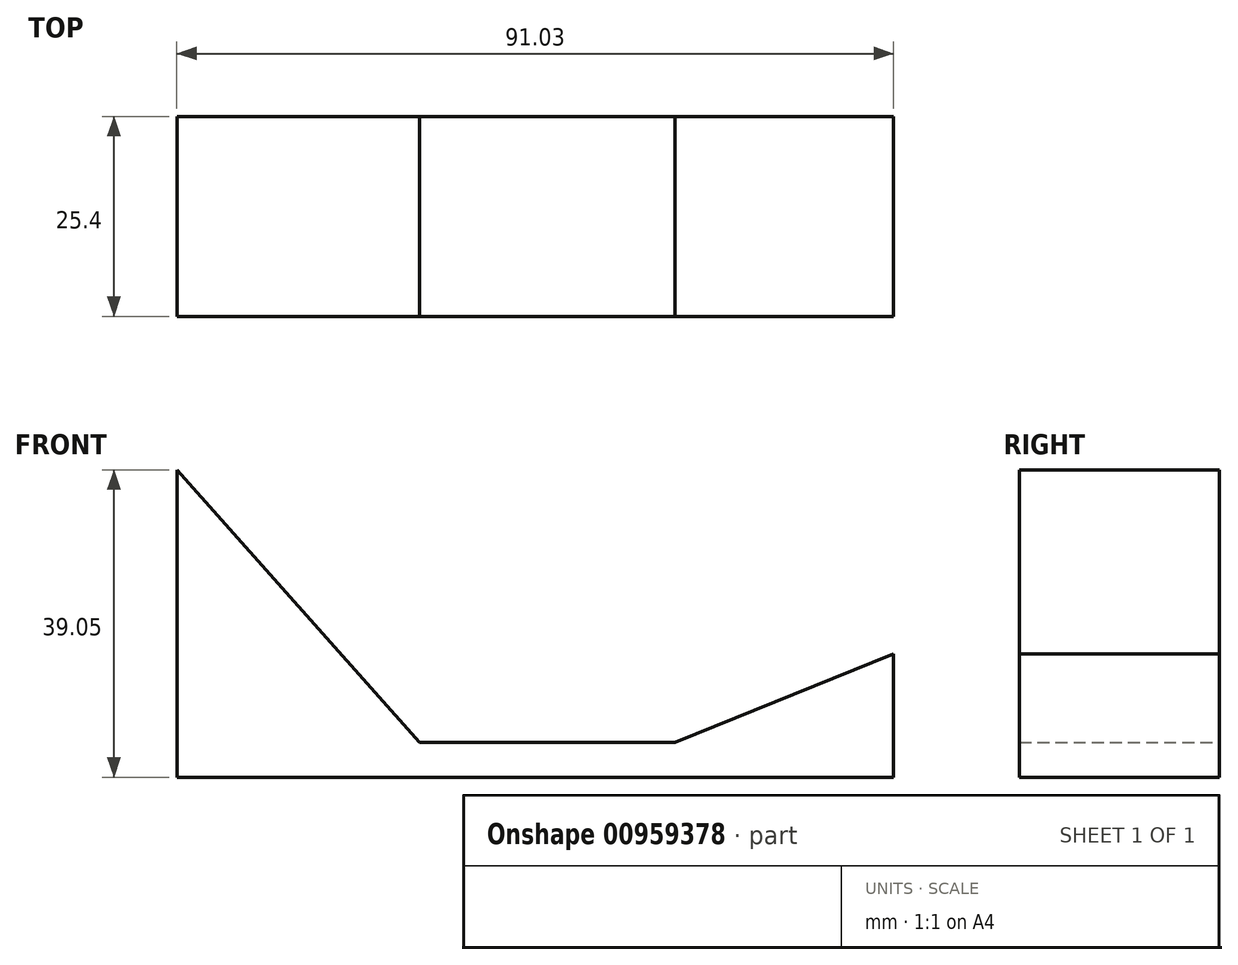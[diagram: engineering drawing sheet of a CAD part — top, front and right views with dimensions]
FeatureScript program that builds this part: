
annotation { "Feature Type Name" : "Feature", "Feature Type Description" : "" }
export const myFeature = defineFeature(function(context is Context, id is Id, definition is map)
    precondition{}
    {
        {
            var Q0;
            Q0=qCreatedBy(makeId("Front.planeOp"),FACE);
            var sketch = newSketch(context, id + "F0", { "sketchPlane" : qUnion([Q0])});
            skLineSegment(sketch, "E0", {"start": v(-42.47, 0) * mm, "end": v(-42.47, 39.05) * mm});
            skLineSegment(sketch, "E1", {"start": v(-42.47, 39.05) * mm, "end": v(-11.67, 4.43) * mm});
            skLineSegment(sketch, "E2", {"start": v(-11.67, 4.43) * mm, "end": v(20.8, 4.43) * mm});
            skLineSegment(sketch, "E3", {"start": v(20.8, 4.43) * mm, "end": v(48.56, 15.63) * mm});
            skLineSegment(sketch, "E4", {"start": v(48.56, 15.63) * mm, "end": v(48.56, 0) * mm});
            skLineSegment(sketch, "E5", {"start": v(48.56, 0) * mm, "end": v(-42.47, 0) * mm});
            skSolve(sketch);
        }
        {
            var Q0;
            Q0 = qSketchRegion(id + "F0", true);
            extrude(context, id + "F1", {"entities" : qUnion([Q0]), "endBound" : BoundingType.SYMMETRIC, "depth" : 25.4 * mm, "offsetDistance" : 25.4 * mm});
        }
    });
